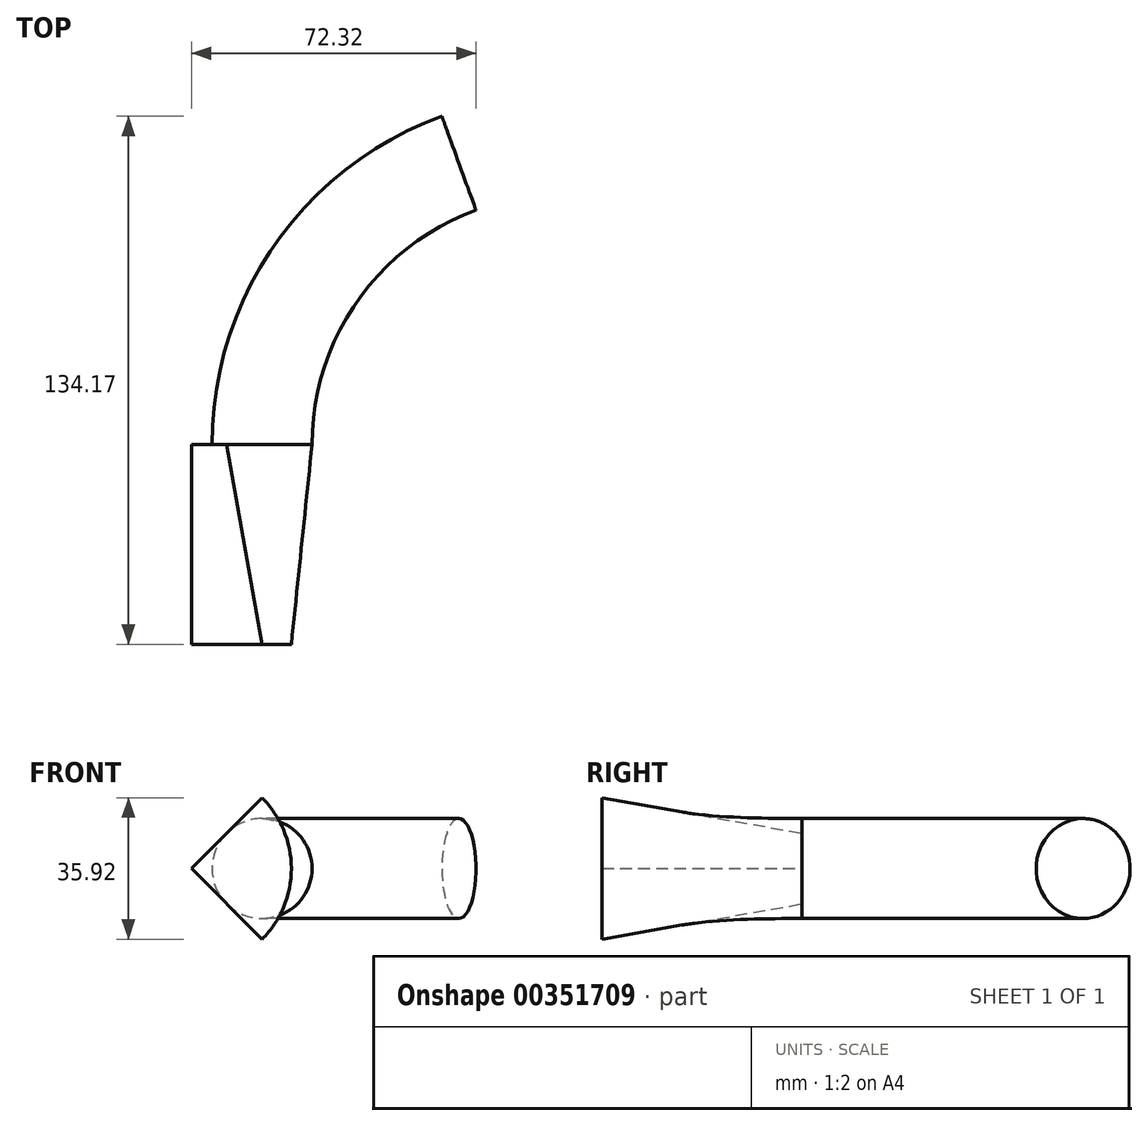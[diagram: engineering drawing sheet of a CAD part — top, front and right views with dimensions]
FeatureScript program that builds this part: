
annotation { "Feature Type Name" : "Feature", "Feature Type Description" : "" }
export const myFeature = defineFeature(function(context is Context, id is Id, definition is map)
    precondition{}
    {
        {
            var Q0;
            Q0=qCreatedBy(makeId("Front.planeOp"),FACE);
            var sketch = newSketch(context, id + "F0", { "sketchPlane" : qUnion([Q0])});
            skArc(sketch, "E0", {"start": v(17.96, -17.96) * mm, "mid": v(25.4, 0) * mm, "end": v(17.96, 17.96) * mm});
            skLineSegment(sketch, "E1", {"start": v(17.96, -17.96) * mm, "end": v(0, 0) * mm});
            skPoint(sketch, "E2.orphan", {"position": v(43.08, 0) * mm});
            skPoint(sketch, "E3.orphan", {"position": v(0, -48.64) * mm});
            skLineSegment(sketch, "E4", {"start": v(0, 0) * mm, "end": v(17.96, 17.96) * mm});
            skSolve(sketch);
        }
        {
            var Q0;
            Q0=qCreatedBy(makeId("Front.planeOp"),FACE);
            cPlane(context, id + "F1", {"entities" : qUnion([Q0]), "cplaneType" : CPlaneType.OFFSET, "offset" : 50.8 * mm, "oppositeDirection" : true, "width" : 152.4 * mm, "height" : 152.4 * mm});
        }
        {
            var Q0;
            Q0=qCreatedBy(id+"F1.planeOp",FACE);
            var sketch = newSketch(context, id + "F2", { "sketchPlane" : qUnion([Q0])});
            skCircle(sketch, "E5", {"center": v(17.96, 0) * mm, "radius": 12.7 * mm});
            skPoint(sketch, "E6.center", {"position": v(0, 0) * mm});
            skPoint(sketch, "E7.0", {"position": v(8.98, 8.98) * mm});
            skPoint(sketch, "E8.0", {"position": v(8.98, -8.98) * mm});
            skSolve(sketch);
        }
        {
            var Q0;
            Q0=qCreatedBy(makeId("Top.planeOp"),FACE);
            var sketch = newSketch(context, id + "F3", { "sketchPlane" : qUnion([Q0])});
            skArc(sketch, "E9", {"start": v(67.92, 122.4) * mm, "mid": v(31.56, 94.5) * mm, "end": v(17.78, 50.8) * mm});
            skSolve(sketch);
        }
        {
            var Q0;
            Q0=qCreatedBy(id+"F1.planeOp",FACE);
            var sketch = newSketch(context, id + "F4", { "sketchPlane" : qUnion([Q0])});
            skArc(sketch, "E10.0", {"start": v(8.98, -8.98) * mm, "mid": v(30.66, 0) * mm, "end": v(8.98, 8.98) * mm});
            skLineSegment(sketch, "E11", {"start": v(0, 0) * mm, "end": v(8.98, -8.98) * mm});
            skLineSegment(sketch, "E12", {"start": v(0, 0) * mm, "end": v(8.98, 8.98) * mm});
            skSolve(sketch);
        }
        {
            var Q0;
            Q0=makeQuery(id+"F0.imprint","IMPRINT",FACE,{"disambiguationData":[TD([[makeQuery(id+"F0.imprint","IMPRINT",EDGE,{"derivedFrom":sQuery(id+"F0.wireOp",EDGE,"E0")}),1.0]])]});
            var Q1;
            Q1=makeQuery(id+"F4.imprint","IMPRINT",FACE,{"disambiguationData":[TD([[makeQuery(id+"F4.imprint","IMPRINT",EDGE,{"derivedFrom":sQuery(id+"F4.wireOp",EDGE,"E10.0")}),1.0]])]});
            loft(context, id + "F5", {"sheetProfilesArray" : [{ "sheetProfileEntities" : qUnion([Q0]) }, { "sheetProfileEntities" : qUnion([Q1]) }]});
        }
        {
            var Q0;
            Q0=makeQuery(id+"F2.imprint","IMPRINT",FACE,{"disambiguationData":[TD([[makeQuery(id+"F2.imprint","IMPRINT",EDGE,{"derivedFrom":sQuery(id+"F2.wireOp",EDGE,"E5")}),1.0]])]});
            var Q1;
            Q1=sQuery(id+"F3.wireOp",EDGE,"E9");
            sweep(context, id + "F6", {"operationType" : NewBodyOperationType.ADD, "profiles" : qUnion([Q0]), "path" : qUnion([Q1])});
        }
    });
